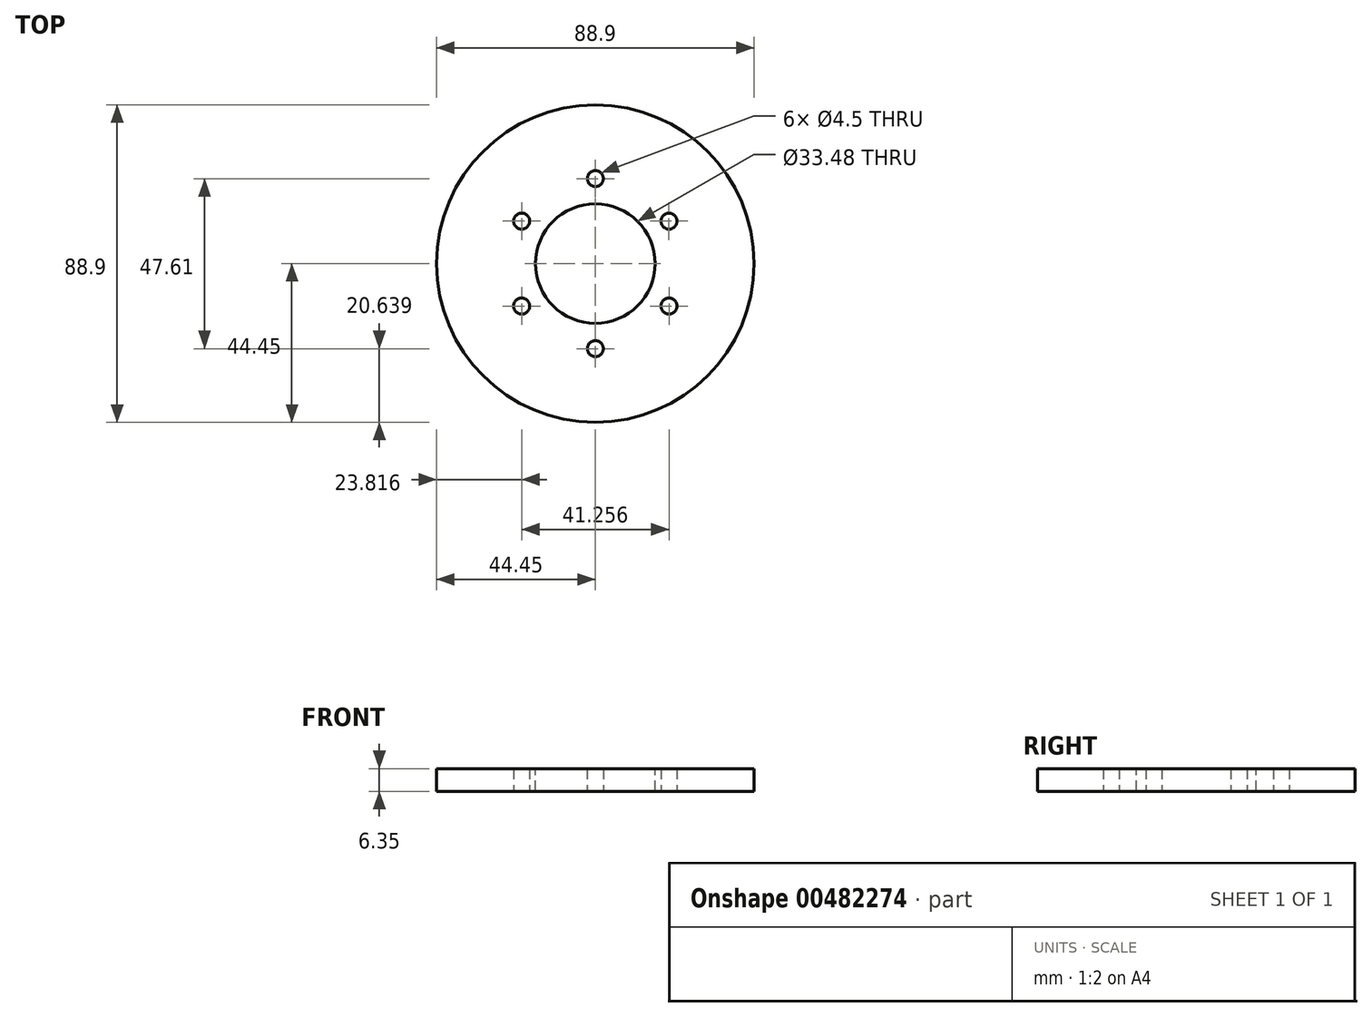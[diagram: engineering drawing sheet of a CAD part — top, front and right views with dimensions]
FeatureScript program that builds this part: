
annotation { "Feature Type Name" : "Feature", "Feature Type Description" : "" }
export const myFeature = defineFeature(function(context is Context, id is Id, definition is map)
    precondition{}
    {
        {
            var Q0;
            Q0=qCreatedBy(makeId("Top.planeOp"),FACE);
            var sketch = newSketch(context, id + "F0", { "sketchPlane" : qUnion([Q0])});
            skCircle(sketch, "E0", {"center": v(0, 0) * mm, "radius": 44.45 * mm});
            skSolve(sketch);
        }
        {
            var Q0;
            Q0=makeQuery(id+"F0.imprint","IMPRINT",FACE,{"disambiguationData":[TD([[makeQuery(id+"F0.imprint","IMPRINT",EDGE,{"derivedFrom":sQuery(id+"F0.wireOp",EDGE,"E0")}),1.0]])]});
            extrude(context, id + "F1", {"entities" : qUnion([Q0]), "depth" : 6.35 * mm});
        }
        {
            var Q0;
            Q0=makeQuery(id+"F1.opExtrude","CAP_FACE",FACE,{"disambiguationData":[OSD([sQuery(id+"F0.wireOp",EDGE,"E0")])],"isStart":false});
            var sketch = newSketch(context, id + "F2", { "sketchPlane" : qUnion([Q0])});
            skCircle(sketch, "E1", {"center": v(0, 0) * mm, "radius": 16.74 * mm});
            skSolve(sketch);
        }
        {
            var Q0;
            Q0=makeQuery(id+"F2.imprint","IMPRINT",FACE,{"disambiguationData":[TD([[makeQuery(id+"F2.imprint","IMPRINT",EDGE,{"derivedFrom":sQuery(id+"F2.wireOp",EDGE,"E1")}),1.0]])]});
            extrude(context, id + "F3", {"entities" : qUnion([Q0]), "operationType" : NewBodyOperationType.REMOVE, "oppositeDirection" : true, "depth" : 6.35 * mm});
        }
        {
            var Q0;
            Q0=qCreatedBy(makeId("Top.planeOp"),FACE);
            var sketch = newSketch(context, id + "F4", { "sketchPlane" : qUnion([Q0])});
            skCircle(sketch, "E2", {"center": v(20.62, -11.9) * mm, "radius": 2.16 * mm});
            skSolve(sketch);
        }
        {
            var Q0;
            Q0=qCreatedBy(makeId("Top.planeOp"),FACE);
            var sketch = newSketch(context, id + "F5", { "sketchPlane" : qUnion([Q0])});
            skCircle(sketch, "E3", {"center": v(20.61, 11.91) * mm, "radius": 2.16 * mm});
            skSolve(sketch);
        }
        {
            var Q0;
            Q0=qCreatedBy(makeId("Top.planeOp"),FACE);
            var sketch = newSketch(context, id + "F6", { "sketchPlane" : qUnion([Q0])});
            skCircle(sketch, "E4", {"center": v(0, 23.8) * mm, "radius": 2.16 * mm});
            skSolve(sketch);
        }
        {
            var Q0;
            Q0=qCreatedBy(makeId("Top.planeOp"),FACE);
            var sketch = newSketch(context, id + "F7", { "sketchPlane" : qUnion([Q0])});
            skCircle(sketch, "E5", {"center": v(-20.62, 11.9) * mm, "radius": 2.16 * mm});
            skSolve(sketch);
        }
        {
            var Q0;
            Q0=qCreatedBy(makeId("Top.planeOp"),FACE);
            var sketch = newSketch(context, id + "F8", { "sketchPlane" : qUnion([Q0])});
            skCircle(sketch, "E6", {"center": v(-20.63, -11.9) * mm, "radius": 2.16 * mm});
            skSolve(sketch);
        }
        {
            var Q0;
            Q0=qCreatedBy(makeId("Top.planeOp"),FACE);
            var sketch = newSketch(context, id + "F9", { "sketchPlane" : qUnion([Q0])});
            skCircle(sketch, "E7", {"center": v(0, -23.81) * mm, "radius": 2.16 * mm});
            skSolve(sketch);
        }
        {
            var Q0;
            Q0=sQuery(id+"F6.wireOp",VERTEX,"E4.center");
            var Q1;
            Q1=makeQuery(id+"F1.opExtrude","SWEPT_BODY",BODY,{"disambiguationData":[OSD([sQuery(id+"F0.wireOp",EDGE,"E0")])]});
            hole(context, id + "F10", {"style" : HoleStyle.SIMPLE, "endStyle" : HoleEndStyle.THROUGH, "oppositeDirection" : true, "standardTappedOrClearance" : lookupTablePath({ "standard" : "ANSI", "fit" : "Normal (ASME)", "size" : "#8", "type" : "Clearance" }), "standardBlindInLast" : lookupTablePath({ "fit" : "Free", "standard" : "ANSI", "size" : "#8", "type" : "Clearance" }), "holeDiameter" : 4.5 * mm, "isTappedThrough" : true, "tappedDepth" : 12.7 * mm, "tapClearance" : 3, "locations" : qUnion([Q0]), "scope" : qUnion([Q1])});
        }
        {
            var Q0;
            Q0=sQuery(id+"F7.wireOp",VERTEX,"E5.center");
            var Q1;
            Q1=makeQuery(id+"F1.opExtrude","SWEPT_BODY",BODY,{"disambiguationData":[OSD([sQuery(id+"F0.wireOp",EDGE,"E0")])]});
            hole(context, id + "F11", {"style" : HoleStyle.SIMPLE, "endStyle" : HoleEndStyle.THROUGH, "oppositeDirection" : true, "standardTappedOrClearance" : lookupTablePath({ "standard" : "ANSI", "fit" : "Normal (ASME)", "size" : "#8", "type" : "Clearance" }), "standardBlindInLast" : lookupTablePath({ "fit" : "Free", "standard" : "ANSI", "size" : "#8", "type" : "Clearance" }), "holeDiameter" : 4.5 * mm, "isTappedThrough" : true, "tappedDepth" : 12.7 * mm, "tapClearance" : 3, "locations" : qUnion([Q0]), "scope" : qUnion([Q1])});
        }
        {
            var Q0;
            Q0=sQuery(id+"F5.wireOp",VERTEX,"E3.center");
            var Q1;
            Q1=makeQuery(id+"F1.opExtrude","SWEPT_BODY",BODY,{"disambiguationData":[OSD([sQuery(id+"F0.wireOp",EDGE,"E0")])]});
            hole(context, id + "F12", {"style" : HoleStyle.SIMPLE, "endStyle" : HoleEndStyle.THROUGH, "oppositeDirection" : true, "standardTappedOrClearance" : lookupTablePath({ "standard" : "ANSI", "fit" : "Normal (ASME)", "size" : "#8", "type" : "Clearance" }), "standardBlindInLast" : lookupTablePath({ "fit" : "Free", "standard" : "ANSI", "size" : "#8", "type" : "Clearance" }), "holeDiameter" : 4.5 * mm, "isTappedThrough" : true, "tappedDepth" : 12.7 * mm, "tapClearance" : 3, "locations" : qUnion([Q0]), "scope" : qUnion([Q1])});
        }
        {
            var Q0;
            Q0=sQuery(id+"F8.wireOp",VERTEX,"E6.center");
            var Q1;
            Q1=makeQuery(id+"F1.opExtrude","SWEPT_BODY",BODY,{"disambiguationData":[OSD([sQuery(id+"F0.wireOp",EDGE,"E0")])]});
            hole(context, id + "F13", {"style" : HoleStyle.SIMPLE, "endStyle" : HoleEndStyle.THROUGH, "oppositeDirection" : true, "standardTappedOrClearance" : lookupTablePath({ "standard" : "ANSI", "fit" : "Normal (ASME)", "size" : "#8", "type" : "Clearance" }), "standardBlindInLast" : lookupTablePath({ "fit" : "Free", "standard" : "ANSI", "size" : "#8", "type" : "Clearance" }), "holeDiameter" : 4.5 * mm, "isTappedThrough" : true, "tappedDepth" : 12.7 * mm, "tapClearance" : 3, "locations" : qUnion([Q0]), "scope" : qUnion([Q1])});
        }
        {
            var Q0;
            Q0=sQuery(id+"F4.wireOp",VERTEX,"E2.center");
            var Q1;
            Q1=makeQuery(id+"F1.opExtrude","SWEPT_BODY",BODY,{"disambiguationData":[OSD([sQuery(id+"F0.wireOp",EDGE,"E0")])]});
            hole(context, id + "F14", {"style" : HoleStyle.SIMPLE, "endStyle" : HoleEndStyle.THROUGH, "oppositeDirection" : true, "standardTappedOrClearance" : lookupTablePath({ "standard" : "ANSI", "fit" : "Normal (ASME)", "size" : "#8", "type" : "Clearance" }), "standardBlindInLast" : lookupTablePath({ "fit" : "Free", "standard" : "ANSI", "size" : "#8", "type" : "Clearance" }), "holeDiameter" : 4.5 * mm, "isTappedThrough" : true, "tappedDepth" : 12.7 * mm, "tapClearance" : 3, "locations" : qUnion([Q0]), "scope" : qUnion([Q1])});
        }
        {
            var Q0;
            Q0=sQuery(id+"F9.wireOp",VERTEX,"E7.center");
            var Q1;
            Q1=makeQuery(id+"F1.opExtrude","SWEPT_BODY",BODY,{"disambiguationData":[OSD([sQuery(id+"F0.wireOp",EDGE,"E0")])]});
            hole(context, id + "F15", {"style" : HoleStyle.SIMPLE, "endStyle" : HoleEndStyle.THROUGH, "oppositeDirection" : true, "standardTappedOrClearance" : lookupTablePath({ "standard" : "ANSI", "fit" : "Normal (ASME)", "size" : "#8", "type" : "Clearance" }), "standardBlindInLast" : lookupTablePath({ "fit" : "Free", "standard" : "ANSI", "size" : "#8", "type" : "Clearance" }), "holeDiameter" : 4.5 * mm, "isTappedThrough" : true, "tappedDepth" : 12.7 * mm, "tapClearance" : 3, "locations" : qUnion([Q0]), "scope" : qUnion([Q1])});
        }
    });
